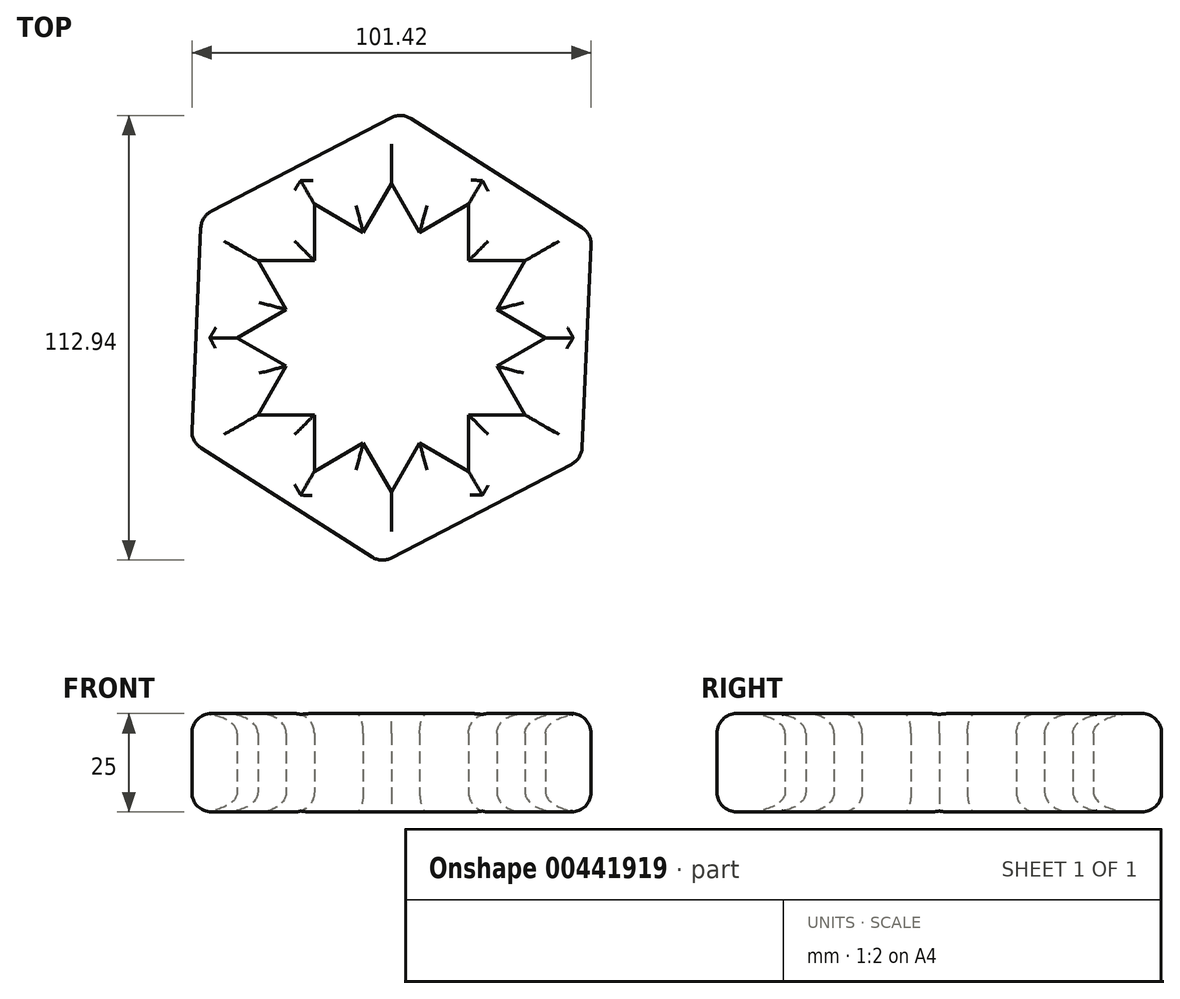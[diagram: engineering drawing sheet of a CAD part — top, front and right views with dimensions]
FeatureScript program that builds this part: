
annotation { "Feature Type Name" : "Feature", "Feature Type Description" : "" }
export const myFeature = defineFeature(function(context is Context, id is Id, definition is map)
    precondition{}
    {
        {
            var Q0;
            Q0=qCreatedBy(makeId("Top.planeOp"),FACE);
            var sketch = newSketch(context, id + "F0", { "sketchPlane" : qUnion([Q0])});
            skCircle(sketch, "E0.cCircle", {"center": v(0, 0) * mm, "radius": 19.59 * mm, "construction": true});
            skLineSegment(sketch, "E0.0", {"start": v(19.59, 33.93) * mm, "end": v(19.59, -33.93) * mm});
            skLineSegment(sketch, "E0.1", {"start": v(19.59, -33.93) * mm, "end": v(-39.18, 0) * mm});
            skLineSegment(sketch, "E0.2", {"start": v(-39.18, 0) * mm, "end": v(19.59, 33.93) * mm});
            skPoint(sketch, "E0.0.midPoint", {"position": v(19.59, 0) * mm});
            skLineSegment(sketch, "E1.0", {"start": v(-19.59, -33.93) * mm, "end": v(-19.59, 33.93) * mm});
            skLineSegment(sketch, "E1.1", {"start": v(-19.59, 33.93) * mm, "end": v(39.18, 0) * mm});
            skLineSegment(sketch, "E1.2", {"start": v(39.18, 0) * mm, "end": v(-19.59, -33.93) * mm});
            skPoint(sketch, "E1.0.midPoint", {"position": v(-19.59, 0) * mm});
            skLineSegment(sketch, "E2.0", {"start": v(0, 39.18) * mm, "end": v(33.93, -19.59) * mm});
            skLineSegment(sketch, "E2.1", {"start": v(33.93, -19.59) * mm, "end": v(-33.93, -19.59) * mm});
            skLineSegment(sketch, "E2.2", {"start": v(-33.93, -19.59) * mm, "end": v(0, 39.18) * mm});
            skPoint(sketch, "E2.0.midPoint", {"position": v(16.96, 9.8) * mm});
            skLineSegment(sketch, "E3.0", {"start": v(33.93, 19.59) * mm, "end": v(0, -39.18) * mm});
            skLineSegment(sketch, "E3.1", {"start": v(0, -39.18) * mm, "end": v(-33.93, 19.59) * mm});
            skLineSegment(sketch, "E3.2", {"start": v(-33.93, 19.59) * mm, "end": v(33.93, 19.59) * mm});
            skPoint(sketch, "E3.0.midPoint", {"position": v(16.96, -9.8) * mm});
            skCircle(sketch, "E4.cCircle", {"center": v(0, 0) * mm, "radius": 49.62 * mm, "construction": true});
            skLineSegment(sketch, "E4.0", {"start": v(-50.84, -26.42) * mm, "end": v(-48.3, 30.82) * mm});
            skLineSegment(sketch, "E4.1", {"start": v(-48.3, 30.82) * mm, "end": v(2.54, 57.24) * mm});
            skLineSegment(sketch, "E4.2", {"start": v(2.54, 57.24) * mm, "end": v(50.84, 26.42) * mm});
            skLineSegment(sketch, "E4.3", {"start": v(50.84, 26.42) * mm, "end": v(48.3, -30.82) * mm});
            skLineSegment(sketch, "E4.4", {"start": v(48.3, -30.82) * mm, "end": v(-2.54, -57.24) * mm});
            skLineSegment(sketch, "E4.5", {"start": v(-2.54, -57.24) * mm, "end": v(-50.84, -26.42) * mm});
            skPoint(sketch, "E4.0.midPoint", {"position": v(-49.57, 2.2) * mm});
            skSolve(sketch);
        }
        {
            var Q0;
            Q0 = qSketchRegion(id + "F0", true);
            extrude(context, id + "F1", {"entities" : qUnion([Q0]), "depth" : 25 * mm});
        }
        {
            var Q0;
            Q0=makeQuery(id+"F1.opExtrude","CAP_EDGE",EDGE,{"disambiguationData":[OSD([sQuery(id+"F0.wireOp",EDGE,"E4.5")])],"isStart":false});
            var Q1;
            Q1=makeQuery(id+"F1.opExtrude","CAP_EDGE",EDGE,{"disambiguationData":[OSD([sQuery(id+"F0.wireOp",EDGE,"E4.5")])],"isStart":true});
            var Q2;
            Q2=makeQuery(id+"F1.opExtrude","CAP_EDGE",EDGE,{"disambiguationData":[OSD([sQuery(id+"F0.wireOp",EDGE,"E4.0")])],"isStart":false});
            var Q3;
            {var subQ0=sQuery(id+"F0.wireOp",EDGE,"E0.2");Q3=makeQuery(id+"F1.opExtrude","CAP_EDGE",EDGE,{"disambiguationData":[OSD([subQ0]),TDD([makeQuery(id+"F0.imprint","IMPRINT",EDGE,{"disambiguationData":[TD([[makeQuery(id+"F0.imprint","INTERSECT",VERTEX,{"derivedFrom":[sQuery(id+"F0.wireOp",EDGE,"E0.1"),subQ0]}),-1.0]])],"derivedFrom":subQ0})])],"isStart":false});}
            var Q4;
            Q4=makeQuery(id+"F1.opExtrude","CAP_FACE",FACE,{"disambiguationData":[OSD([sQuery(id+"F0.wireOp",EDGE,"E0.0"),sQuery(id+"F0.wireOp",EDGE,"E0.1"),sQuery(id+"F0.wireOp",EDGE,"E0.2"),sQuery(id+"F0.wireOp",EDGE,"E1.0"),sQuery(id+"F0.wireOp",EDGE,"E1.1"),sQuery(id+"F0.wireOp",EDGE,"E1.2"),sQuery(id+"F0.wireOp",EDGE,"E2.0"),sQuery(id+"F0.wireOp",EDGE,"E2.1"),sQuery(id+"F0.wireOp",EDGE,"E2.2"),sQuery(id+"F0.wireOp",EDGE,"E3.0"),sQuery(id+"F0.wireOp",EDGE,"E3.1"),sQuery(id+"F0.wireOp",EDGE,"E3.2"),sQuery(id+"F0.wireOp",EDGE,"E4.0"),sQuery(id+"F0.wireOp",EDGE,"E4.1"),sQuery(id+"F0.wireOp",EDGE,"E4.2"),sQuery(id+"F0.wireOp",EDGE,"E4.3"),sQuery(id+"F0.wireOp",EDGE,"E4.4"),sQuery(id+"F0.wireOp",EDGE,"E4.5")])],"isStart":false});
            var Q5;
            {var subQ0=sQuery(id+"F0.wireOp",EDGE,"E3.2");Q5=makeQuery(id+"F1.opExtrude","CAP_EDGE",EDGE,{"disambiguationData":[OSD([subQ0]),TDD([makeQuery(id+"F0.imprint","IMPRINT",EDGE,{"disambiguationData":[TD([[makeQuery(id+"F0.imprint","INTERSECT",VERTEX,{"derivedFrom":[sQuery(id+"F0.wireOp",EDGE,"E3.1"),subQ0]}),-1.0]])],"derivedFrom":subQ0})])],"isStart":false});}
            var Q6;
            {var subQ0=sQuery(id+"F0.wireOp",EDGE,"E2.2");Q6=makeQuery(id+"F1.opExtrude","CAP_EDGE",EDGE,{"disambiguationData":[OSD([subQ0]),TDD([makeQuery(id+"F0.imprint","IMPRINT",EDGE,{"disambiguationData":[TD([[makeQuery(id+"F0.imprint","INTERSECT",VERTEX,{"derivedFrom":[sQuery(id+"F0.wireOp",EDGE,"E2.0"),subQ0]}),1.0]])],"derivedFrom":subQ0})])],"isStart":true});}
            var Q7;
            {var subQ0=sQuery(id+"F0.wireOp",EDGE,"E2.0");Q7=makeQuery(id+"F1.opExtrude","CAP_EDGE",EDGE,{"disambiguationData":[OSD([subQ0]),TDD([makeQuery(id+"F0.imprint","IMPRINT",EDGE,{"disambiguationData":[TD([[makeQuery(id+"F0.imprint","INTERSECT",VERTEX,{"derivedFrom":[subQ0,sQuery(id+"F0.wireOp",EDGE,"E2.2")]}),-1.0]])],"derivedFrom":subQ0})])],"isStart":true});}
            var Q8;
            Q8=makeQuery(id+"F1.opExtrude","CAP_FACE",FACE,{"disambiguationData":[OSD([sQuery(id+"F0.wireOp",EDGE,"E0.0"),sQuery(id+"F0.wireOp",EDGE,"E0.1"),sQuery(id+"F0.wireOp",EDGE,"E0.2"),sQuery(id+"F0.wireOp",EDGE,"E1.0"),sQuery(id+"F0.wireOp",EDGE,"E1.1"),sQuery(id+"F0.wireOp",EDGE,"E1.2"),sQuery(id+"F0.wireOp",EDGE,"E2.0"),sQuery(id+"F0.wireOp",EDGE,"E2.1"),sQuery(id+"F0.wireOp",EDGE,"E2.2"),sQuery(id+"F0.wireOp",EDGE,"E3.0"),sQuery(id+"F0.wireOp",EDGE,"E3.1"),sQuery(id+"F0.wireOp",EDGE,"E3.2"),sQuery(id+"F0.wireOp",EDGE,"E4.0"),sQuery(id+"F0.wireOp",EDGE,"E4.1"),sQuery(id+"F0.wireOp",EDGE,"E4.2"),sQuery(id+"F0.wireOp",EDGE,"E4.3"),sQuery(id+"F0.wireOp",EDGE,"E4.4"),sQuery(id+"F0.wireOp",EDGE,"E4.5")])],"isStart":true});
            var Q9;
            Q9=makeQuery(id+"F1.opExtrude","SWEPT_EDGE",EDGE,{"disambiguationData":[OSD([sQuery(id+"F0.wireOp",EDGE,"E4.3"),sQuery(id+"F0.wireOp",EDGE,"E4.4")])]});
            var Q10;
            Q10=makeQuery(id+"F1.opExtrude","SWEPT_EDGE",EDGE,{"disambiguationData":[OSD([sQuery(id+"F0.wireOp",EDGE,"E4.2"),sQuery(id+"F0.wireOp",EDGE,"E4.3")])]});
            var Q11;
            Q11=makeQuery(id+"F1.opExtrude","SWEPT_EDGE",EDGE,{"disambiguationData":[OSD([sQuery(id+"F0.wireOp",EDGE,"E4.1"),sQuery(id+"F0.wireOp",EDGE,"E4.2")])]});
            var Q12;
            Q12=makeQuery(id+"F1.opExtrude","SWEPT_EDGE",EDGE,{"disambiguationData":[OSD([sQuery(id+"F0.wireOp",EDGE,"E4.0"),sQuery(id+"F0.wireOp",EDGE,"E4.1")])]});
            var Q13;
            Q13=makeQuery(id+"F1.opExtrude","SWEPT_EDGE",EDGE,{"disambiguationData":[OSD([sQuery(id+"F0.wireOp",EDGE,"E4.0"),sQuery(id+"F0.wireOp",EDGE,"E4.5")])]});
            var Q14;
            Q14=makeQuery(id+"F1.opExtrude","SWEPT_FACE",FACE,{"disambiguationData":[OSD([sQuery(id+"F0.wireOp",EDGE,"E4.5")])]});
            fillet(context, id + "F2", {"entities" : qUnion([Q0, Q1, Q2, Q3, Q4, Q5, Q6, Q7, Q8, Q9, Q10, Q11, Q12, Q13, Q14]), "radius" : 5 * mm, "tangentPropagation" : true, "allowEdgeOverflow" : false});
        }
    });
